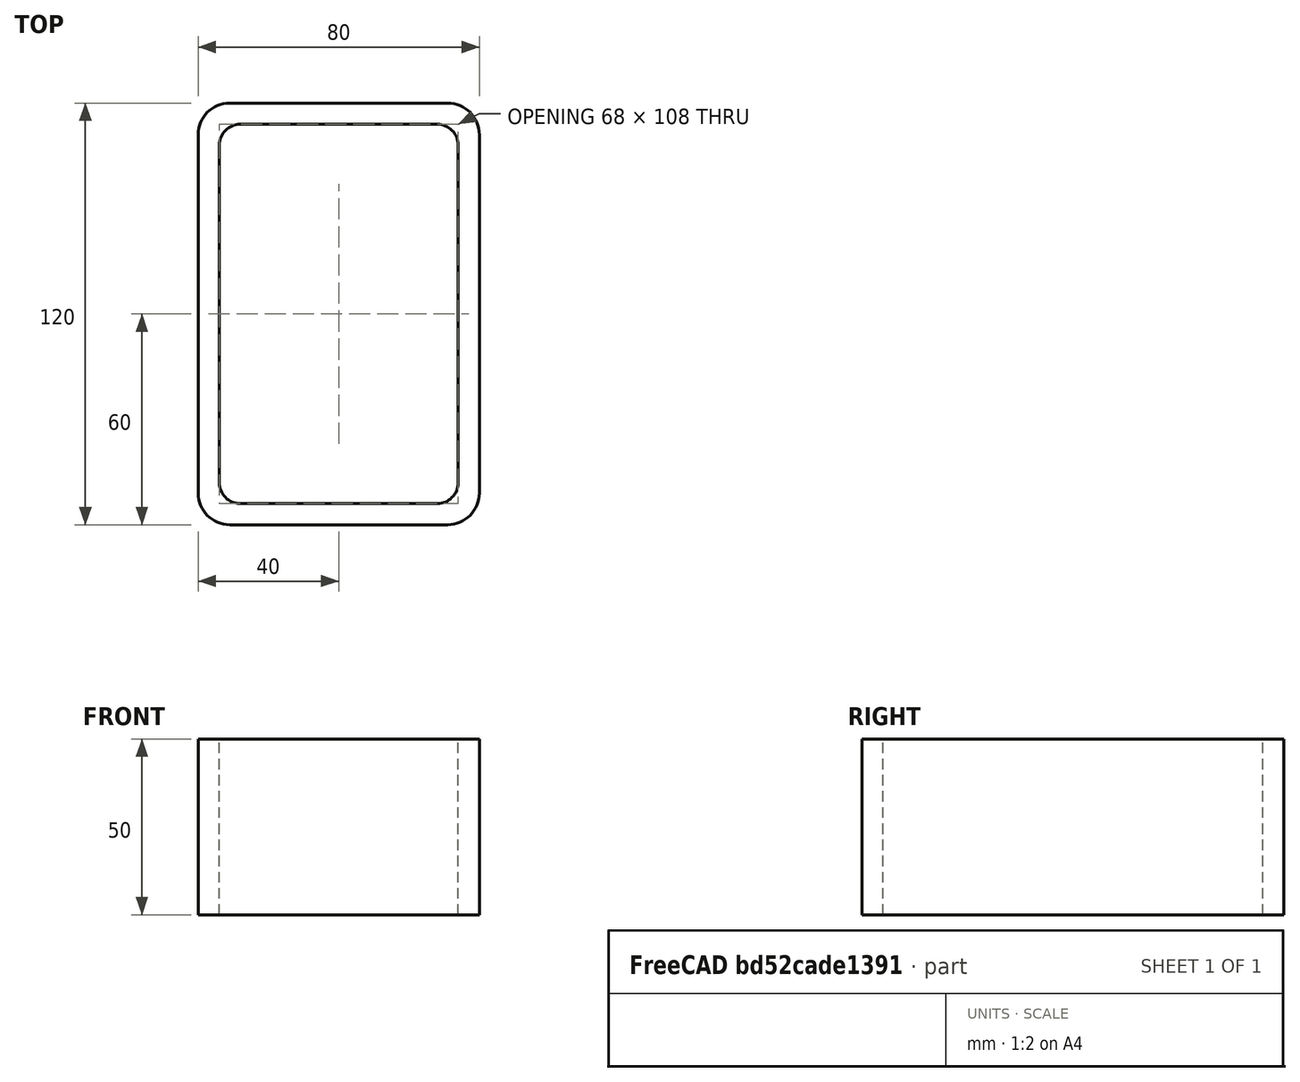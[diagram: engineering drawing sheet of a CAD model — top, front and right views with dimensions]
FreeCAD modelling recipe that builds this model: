
FCSTD DOCUMENT  (FreeCAD 0.15R4671 (Git))
Label: Rectangular hollow section 120x80x6 EN10219 S235JRH
License: All rights reserved
LicenseURL: http://en.wikipedia.org/wiki/All_rights_reserved
objects: Sketcher::SketchObject×1, Part::Extrusion×1
note: 2 computed .brp shape members not serialized (recipe doc carries the construction recipe); baked Part::Feature solids carry a one-line shape summary decoded from their .brp

FEATURE [Sketcher::SketchObject] Sketch
  sketch-geometry (16):
    g0: LineSegment StartX=-28 StartY=54 StartZ=0 EndX=28 EndY=54 EndZ=0
    g1: LineSegment StartX=34 StartY=48 StartZ=0 EndX=34 EndY=-48 EndZ=0
    g2: LineSegment StartX=28 StartY=-54 StartZ=0 EndX=-28 EndY=-54 EndZ=0
    g3: LineSegment StartX=-34 StartY=-48 StartZ=0 EndX=-34 EndY=48 EndZ=0
    g4: LineSegment StartX=-31 StartY=60 StartZ=0 EndX=31 EndY=60 EndZ=0
    g5: LineSegment StartX=40 StartY=51 StartZ=0 EndX=40 EndY=-51 EndZ=0
    g6: LineSegment StartX=31 StartY=-60 StartZ=0 EndX=-31 EndY=-60 EndZ=0
    g7: LineSegment StartX=-40 StartY=-51 StartZ=0 EndX=-40 EndY=51 EndZ=0
    g8: ArcOfCircle CenterX=-28 CenterY=48 CenterZ=0 NormalX=0 NormalY=0 NormalZ=1 Radius=6 StartAngle=1.5708 EndAngle=3.14159
    g9: ArcOfCircle CenterX=28 CenterY=48 CenterZ=0 NormalX=0 NormalY=0 NormalZ=1 Radius=6 StartAngle=0 EndAngle=1.5708
    g10: ArcOfCircle CenterX=28 CenterY=-48 CenterZ=0 NormalX=0 NormalY=0 NormalZ=1 Radius=6 StartAngle=4.71239 EndAngle=6.28319
    g11: ArcOfCircle CenterX=-28 CenterY=-48 CenterZ=0 NormalX=0 NormalY=0 NormalZ=1 Radius=6 StartAngle=3.14159 EndAngle=4.71239
    g12: ArcOfCircle CenterX=31 CenterY=51 CenterZ=0 NormalX=0 NormalY=0 NormalZ=1 Radius=9 StartAngle=0 EndAngle=1.5708
    g13: ArcOfCircle CenterX=31 CenterY=-51 CenterZ=0 NormalX=0 NormalY=0 NormalZ=1 Radius=9 StartAngle=4.71239 EndAngle=6.28319
    g14: ArcOfCircle CenterX=-31 CenterY=-51 CenterZ=0 NormalX=0 NormalY=0 NormalZ=1 Radius=9 StartAngle=3.14159 EndAngle=4.71239
    g15: ArcOfCircle CenterX=-31 CenterY=51 CenterZ=0 NormalX=0 NormalY=0 NormalZ=1 Radius=9 StartAngle=1.5708 EndAngle=3.14159
  constraints (36):
    c: Horizontal(g2)
    c: Vertical(g3)
    c: Horizontal(g6)
    c: Vertical(g7)
    c: Tangent(g3,g8) = 1.5708
    c: Tangent(g0,g8) = 1.5708
    c: Tangent(g0,g9) = 1.5708
    c: Tangent(g1,g9) = 1.5708
    c: Tangent(g1,g10) = 1.5708
    c: Tangent(g2,g10) = 1.5708
    c: Tangent(g2,g11) = 1.5708
    c: Tangent(g3,g11) = 1.5708
    c: Tangent(g4,g12) = 1.5708
    c: Tangent(g5,g12) = 1.5708
    c: Tangent(g5,g13) = 1.5708
    c: Tangent(g6,g13) = 1.5708
    c: Tangent(g6,g14) = 1.5708
    c: Tangent(g7,g14) = 1.5708
    c: Tangent(g7,g15) = 1.5708
    c: Tangent(g4,g15) = 1.5708
    c: Equal(g9,g8)
    c: Equal(g9,g11)
    c: Equal(g9,g10)
    c: Equal(g12,g15)
    c: Equal(g12,g14)
    c: Equal(g12,g13)
    c: Symmetric(g4,g6,g-1)
    c: Symmetric(g7,g5,g-2)
    c: DistanceY(g4,g6) = -120
    c: DistanceX(g7,g5) = 80
    c: Symmetric(g3,g1,g-2)
    c: Symmetric(g0,g2,g-1)
    c: DistanceY(g0,g4) = 6
    c: DistanceX(g5,g1) = -6
    c: Radius(g9) = 6
    c: Radius(g12) = 9
FEATURE [Part::Extrusion] Extrude  label="Rectangular hollow section 120x80x6 EN10219 S235JRH"
  Base = -> Sketch
  Dir = (0,0,50)
  Solid = true
